# Revit family: IVLB_PML_LF_Briq WM_Plastic
name_source: partatom
category: Lighting Fixtures
units: mm (PartAtom-declared; Revit-internal decimal feet)

## family parameters
Always vertical = Yes
Cut with Voids When Loaded = No
Light Source = No
OmniClass Number = 23.80.70.11.11
OmniClass Title = General Luminaries, Non Directional
Part Type = Normal
Room Calculation Point = No
Round Connector Dimension = Use Diameter
Shared = No
Work Plane-Based = No

## types (6) — shared parameters
Apparent Load = 7 VA
Assembly Code = 63.0
Description = Surface Mounted
IK Value = IK10
IP Value = IP65
IfcExportAs = IfcLightFixtureType
IfcExportType = USERDEFINED
Lamp = LED
Load Classification = Lighting
Luminaire_Body_Material = Select RGB value
Luminous Flux = 840 lm
Manufacturer = Pragmalux - Distrilight
Model = BRIQ
URL = https://www.pragmalux.com
Voltage = 230 V
Wattage Comments = 7W

## per-type parameters (varying)
| type | IES File |
| Briq IP65 C4 Down 7W 800-840lm 3000-4000K 2CCT DALI-2 | Briq Geometry : Briq Up Down IP65 C4 Down 7W 800-840lm Up 3W 400-420lm 3000-4000K 2CCT fase dimbaar |
| Briq IP65 C4 Down 7W 800-840lm 3000-4000K 2CCT Fase Dimbaar | Briq Geometry : Briq IP65 C4 Down 7W 800-840lm 3000-4000K 2CCT Fase Dimbaar |
| Briq IP65 C4 Down 7W 800-840lm 3000-4000K 2CCT | Briq Geometry : Briq IP65 C4 Down 7W 800-840lm 3000-4000K 2CCT |
| Briq Up Down IP65 C4 Down 7W 800-840lm Up 3W 400-420lm 3000-4000K 2CCT DALI | Briq Geometry : Briq Up Down IP65 C4 Down 7W 800-840lm Up 3W 400-420lm 3000-4000K 2CCT DALI |
| Briq Up Down IP65 C4 Down 7W 800-840lm Up 3W 400-420lm 3000-4000K 2CCT fase dimbaar | Briq Geometry : Briq Up Down IP65 C4 Down 7W 800-840lm Up 3W 400-420lm 3000-4000K 2CCT fase dimbaar |
| Briq Up Down IP65 C4 Down 7W 800-840lm Up 3W 400-420lm 3000-4000K 2CCT | Briq Geometry : Briq Up Down IP65 C4 Down 7W 800-840lm Up 3W 400-420lm 3000-4000K 2CCT |

## geometry (parser evidence)
native form markers: Sweep x7
no freeform markers — native parametric forms only
